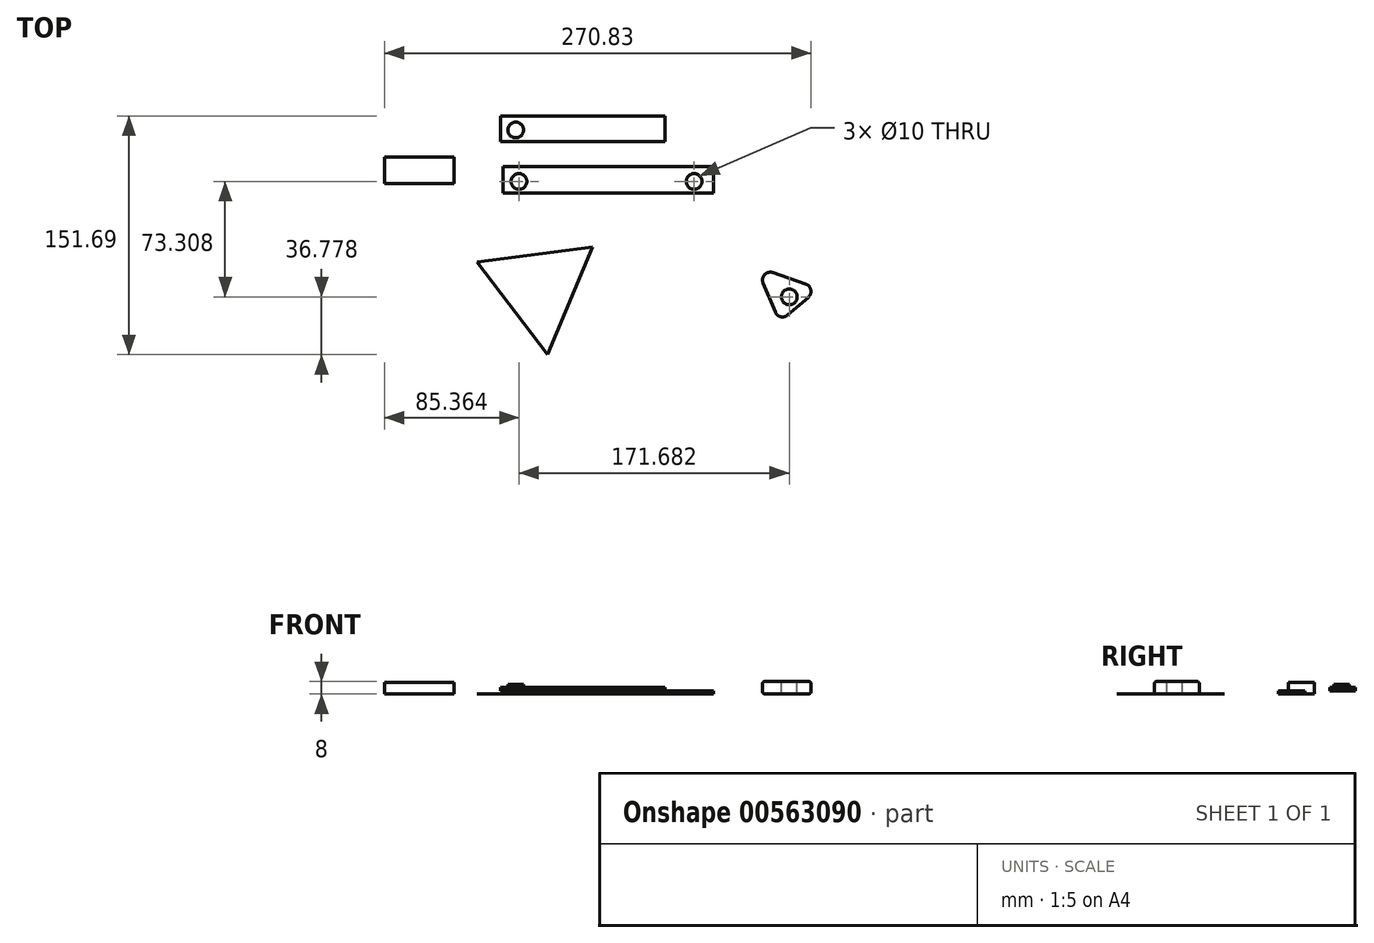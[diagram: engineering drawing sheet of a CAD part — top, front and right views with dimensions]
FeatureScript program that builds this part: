
annotation { "Feature Type Name" : "Feature", "Feature Type Description" : "" }
export const myFeature = defineFeature(function(context is Context, id is Id, definition is map)
    precondition{}
    {
        {
            var Q0;
            Q0=qCreatedBy(makeId("Top.planeOp"),FACE);
            var sketch = newSketch(context, id + "F0", { "sketchPlane" : qUnion([Q0])});
            skLineSegment(sketch, "E0.bottom", {"start": v(-66.17, 23.3) * mm, "end": v(67.43, 23.3) * mm});
            skLineSegment(sketch, "E0.top", {"start": v(-66.17, 6.36) * mm, "end": v(67.43, 6.36) * mm});
            skLineSegment(sketch, "E0.left", {"start": v(-66.17, 23.3) * mm, "end": v(-66.17, 6.36) * mm});
            skLineSegment(sketch, "E0.right", {"start": v(67.43, 23.3) * mm, "end": v(67.43, 6.36) * mm});
            skSolve(sketch);
        }
        {
            var Q0;
            Q0 = qSketchRegion(id + "F0", true);
            extrude(context, id + "F1", {"entities" : qUnion([Q0]), "depth" : 2.1 * mm, "offsetDistance" : 25 * mm});
        }
        {
            var Q0;
            Q0=makeQuery(id+"F1.opExtrude","CAP_FACE",FACE,{"disambiguationData":[OSD([sQuery(id+"F0.wireOp",EDGE,"E0.bottom"),sQuery(id+"F0.wireOp",EDGE,"E0.top"),sQuery(id+"F0.wireOp",EDGE,"E0.left"),sQuery(id+"F0.wireOp",EDGE,"E0.right")])],"isStart":false});
            var sketch = newSketch(context, id + "F2", { "sketchPlane" : qUnion([Q0])});
            skCircle(sketch, "E1", {"center": v(-56.22, 13.84) * mm, "radius": 5 * mm});
            skCircle(sketch, "E2", {"center": v(55.01, 13.84) * mm, "radius": 5 * mm});
            skSolve(sketch);
        }
        {
            var Q0;
            Q0=makeQuery(id+"F2.imprint","IMPRINT",FACE,{"disambiguationData":[TD([[makeQuery(id+"F2.imprint","IMPRINT",EDGE,{"derivedFrom":sQuery(id+"F2.wireOp",EDGE,"E1")}),1.0]])]});
            var Q1;
            Q1=makeQuery(id+"F2.imprint","IMPRINT",FACE,{"disambiguationData":[TD([[makeQuery(id+"F2.imprint","IMPRINT",EDGE,{"derivedFrom":sQuery(id+"F2.wireOp",EDGE,"E2")}),1.0]])]});
            extrude(context, id + "F3", {"entities" : qUnion([Q0, Q1]), "operationType" : NewBodyOperationType.REMOVE, "oppositeDirection" : true, "depth" : 25 * mm, "offsetDistance" : 25 * mm});
        }
        {
            var Q0;
            Q0=makeQuery(id+"F1.opExtrude","CAP_FACE",FACE,{"disambiguationData":[OSD([sQuery(id+"F0.wireOp",EDGE,"E0.bottom"),sQuery(id+"F0.wireOp",EDGE,"E0.top"),sQuery(id+"F0.wireOp",EDGE,"E0.left"),sQuery(id+"F0.wireOp",EDGE,"E0.right")])],"isStart":false});
            var sketch = newSketch(context, id + "F4", { "sketchPlane" : qUnion([Q0])});
            skLineSegment(sketch, "E3.bottom", {"start": v(-67.9, 55.44) * mm, "end": v(36.54, 55.44) * mm});
            skLineSegment(sketch, "E3.top", {"start": v(-67.9, 39.15) * mm, "end": v(36.54, 39.15) * mm});
            skLineSegment(sketch, "E3.left", {"start": v(-67.9, 55.44) * mm, "end": v(-67.9, 39.15) * mm});
            skLineSegment(sketch, "E3.right", {"start": v(36.54, 55.44) * mm, "end": v(36.54, 39.15) * mm});
            skSolve(sketch);
        }
        {
            var Q0;
            Q0=makeQuery(id+"F4.imprint","IMPRINT",FACE,{"disambiguationData":[TD([[makeQuery(id+"F4.imprint","IMPRINT",EDGE,{"derivedFrom":sQuery(id+"F4.wireOp",EDGE,"E3.bottom")}),-1.0]])]});
            extrude(context, id + "F5", {"entities" : qUnion([Q0]), "depth" : 2 * mm, "offsetDistance" : 25 * mm});
        }
        {
            var Q0;
            Q0=makeQuery(id+"F5.opExtrude","CAP_FACE",FACE,{"disambiguationData":[OSD([sQuery(id+"F4.wireOp",EDGE,"E3.bottom"),sQuery(id+"F4.wireOp",EDGE,"E3.top"),sQuery(id+"F4.wireOp",EDGE,"E3.left"),sQuery(id+"F4.wireOp",EDGE,"E3.right")])],"isStart":false});
            var sketch = newSketch(context, id + "F6", { "sketchPlane" : qUnion([Q0])});
            skCircle(sketch, "E4", {"center": v(-58.27, 46.53) * mm, "radius": 5 * mm});
            skSolve(sketch);
        }
        {
            var Q0;
            Q0=makeQuery(id+"F6.imprint","IMPRINT",FACE,{"disambiguationData":[TD([[makeQuery(id+"F6.imprint","IMPRINT",EDGE,{"derivedFrom":sQuery(id+"F6.wireOp",EDGE,"E4")}),1.0]])]});
            extrude(context, id + "F7", {"entities" : qUnion([Q0]), "operationType" : NewBodyOperationType.ADD, "depth" : 2 * mm, "offsetDistance" : 25 * mm});
        }
        {
            var Q0;
            Q0=qCreatedBy(makeId("Top.planeOp"),FACE);
            var sketch = newSketch(context, id + "F8", { "sketchPlane" : qUnion([Q0])});
            skLineSegment(sketch, "E5.bottom", {"start": v(-141.58, 29.35) * mm, "end": v(-97.52, 29.35) * mm});
            skLineSegment(sketch, "E5.top", {"start": v(-141.58, 12.6) * mm, "end": v(-97.52, 12.6) * mm});
            skLineSegment(sketch, "E5.left", {"start": v(-141.58, 29.35) * mm, "end": v(-141.58, 12.6) * mm});
            skLineSegment(sketch, "E5.right", {"start": v(-97.52, 29.35) * mm, "end": v(-97.52, 12.6) * mm});
            skSolve(sketch);
        }
        {
            var Q0;
            Q0=makeQuery(id+"F8.imprint","IMPRINT",FACE,{"disambiguationData":[TD([[makeQuery(id+"F8.imprint","IMPRINT",EDGE,{"derivedFrom":sQuery(id+"F8.wireOp",EDGE,"E5.bottom")}),-1.0]])]});
            extrude(context, id + "F9", {"entities" : qUnion([Q0]), "depth" : 7.2 * mm, "offsetDistance" : 25 * mm});
        }
        {
            var Q0;
            Q0=qCreatedBy(makeId("Top.planeOp"),FACE);
            var sketch = newSketch(context, id + "F10", { "sketchPlane" : qUnion([Q0])});
            skCircle(sketch, "E6.cCircle", {"center": v(-43.55, -53.9) * mm, "radius": 21.36 * mm, "construction": true});
            skLineSegment(sketch, "E6.0", {"start": v(-9.65, -27.9) * mm, "end": v(-37.99, -96.25) * mm});
            skLineSegment(sketch, "E6.1", {"start": v(-37.99, -96.25) * mm, "end": v(-83, -37.53) * mm});
            skLineSegment(sketch, "E6.2", {"start": v(-83, -37.53) * mm, "end": v(-9.65, -27.9) * mm});
            skPoint(sketch, "E6.0.midPoint", {"position": v(-23.82, -62.08) * mm});
            skSolve(sketch);
        }
        {
            var Q0;
            Q0=makeQuery(id+"F10.imprint","IMPRINT",FACE,{"disambiguationData":[TD([[makeQuery(id+"F10.imprint","IMPRINT",EDGE,{"derivedFrom":sQuery(id+"F10.wireOp",EDGE,"E6.0")}),-1.0]])]});
            extrude(context, id + "F11", {"entities" : qUnion([Q0]), "depth" : 0.1 * mm, "offsetDistance" : 25 * mm});
        }
        {
            var Q0;
            Q0=qCreatedBy(makeId("Top.planeOp"),FACE);
            var sketch = newSketch(context, id + "F12", { "sketchPlane" : qUnion([Q0])});
            skLineSegment(sketch, "E7", {"start": v(134.1, -54.12) * mm, "end": v(109.22, -75.58) * mm});
            skLineSegment(sketch, "E8", {"start": v(109.22, -75.58) * mm, "end": v(94.6, -40.47) * mm});
            skLineSegment(sketch, "E9", {"start": v(94.6, -40.47) * mm, "end": v(134.1, -54.12) * mm});
            skSolve(sketch);
        }
        {
            var Q0;
            Q0=makeQuery(id+"F12.imprint","IMPRINT",FACE,{"disambiguationData":[TD([[makeQuery(id+"F12.imprint","IMPRINT",EDGE,{"derivedFrom":sQuery(id+"F12.wireOp",EDGE,"E7")}),-1.0]])]});
            extrude(context, id + "F13", {"entities" : qUnion([Q0]), "depth" : 8 * mm, "offsetDistance" : 25 * mm});
        }
        {
            var Q0;
            Q0=makeQuery(id+"F13.opExtrude","CAP_FACE",FACE,{"disambiguationData":[OSD([sQuery(id+"F12.wireOp",EDGE,"E7"),sQuery(id+"F12.wireOp",EDGE,"E8"),sQuery(id+"F12.wireOp",EDGE,"E9")])],"isStart":false});
            var Q1;
            Q1=makeQuery(id+"F13.opExtrude","CAP_FACE",FACE,{"disambiguationData":[OSD([sQuery(id+"F12.wireOp",EDGE,"E7"),sQuery(id+"F12.wireOp",EDGE,"E8"),sQuery(id+"F12.wireOp",EDGE,"E9")])],"isStart":true});
            fillet(context, id + "F14", {"entities" : qUnion([Q0, Q1]), "radius" : 1.5 * mm, "tangentPropagation" : true, "allowEdgeOverflow" : false});
        }
        {
            var Q0;
            Q0=makeQuery(id+"F14.opFillet","BLEND_EDGE",EDGE,{"blendedFrom":[makeQuery(id+"F13.opExtrude","CAP_EDGE",EDGE,{"disambiguationData":[OSD([sQuery(id+"F12.wireOp",EDGE,"E7")])],"isStart":false}),makeQuery(id+"F13.opExtrude","CAP_EDGE",EDGE,{"disambiguationData":[OSD([sQuery(id+"F12.wireOp",EDGE,"E8")])],"isStart":false})],"blendedInto":[]});
            var Q1;
            Q1=makeQuery(id+"F13.opExtrude","SWEPT_EDGE",EDGE,{"disambiguationData":[OSD([sQuery(id+"F12.wireOp",EDGE,"E7"),sQuery(id+"F12.wireOp",EDGE,"E9")])]});
            var Q2;
            Q2=makeQuery(id+"F14.opFillet","BLEND_EDGE",EDGE,{"blendedFrom":[makeQuery(id+"F13.opExtrude","CAP_EDGE",EDGE,{"disambiguationData":[OSD([sQuery(id+"F12.wireOp",EDGE,"E8")])],"isStart":false}),makeQuery(id+"F13.opExtrude","CAP_EDGE",EDGE,{"disambiguationData":[OSD([sQuery(id+"F12.wireOp",EDGE,"E9")])],"isStart":false})],"blendedInto":[]});
            fillet(context, id + "F15", {"entities" : qUnion([Q0, Q1, Q2]), "radius" : 5 * mm, "tangentPropagation" : true, "allowEdgeOverflow" : false});
        }
        {
            var Q0;
            Q0=makeQuery(id+"F13.opExtrude","CAP_FACE",FACE,{"disambiguationData":[OSD([sQuery(id+"F12.wireOp",EDGE,"E7"),sQuery(id+"F12.wireOp",EDGE,"E8"),sQuery(id+"F12.wireOp",EDGE,"E9")])],"isStart":false});
            var sketch = newSketch(context, id + "F16", { "sketchPlane" : qUnion([Q0])});
            skCircle(sketch, "E10", {"center": v(115.47, -59.47) * mm, "radius": 5 * mm});
            skSolve(sketch);
        }
        {
            var Q0;
            Q0=makeQuery(id+"F16.imprint","IMPRINT",FACE,{"disambiguationData":[TD([[makeQuery(id+"F16.imprint","IMPRINT",EDGE,{"derivedFrom":sQuery(id+"F16.wireOp",EDGE,"E10")}),1.0]])]});
            extrude(context, id + "F17", {"entities" : qUnion([Q0]), "operationType" : NewBodyOperationType.REMOVE, "oppositeDirection" : true, "depth" : 25 * mm, "offsetDistance" : 25 * mm});
        }
    });
